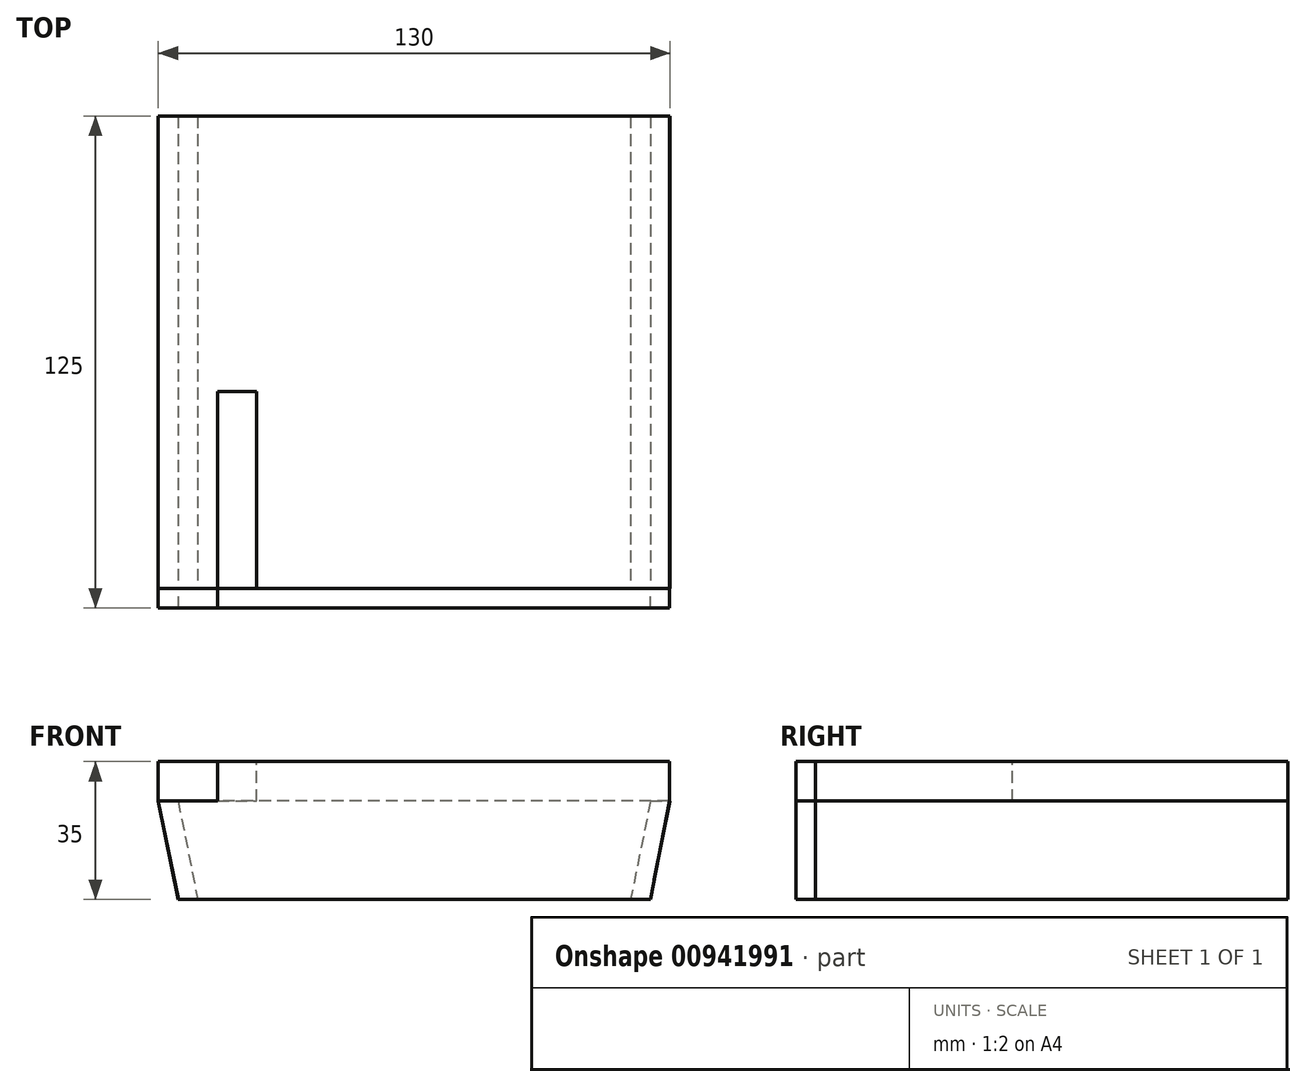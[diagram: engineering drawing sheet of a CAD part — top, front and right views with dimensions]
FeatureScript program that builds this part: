
annotation { "Feature Type Name" : "Feature", "Feature Type Description" : "" }
export const myFeature = defineFeature(function(context is Context, id is Id, definition is map)
    precondition{}
    {
        {
            var Q0;
            Q0=qCreatedBy(makeId("Top.planeOp"),FACE);
            var sketch = newSketch(context, id + "F0", { "sketchPlane" : qUnion([Q0])});
            skLineSegment(sketch, "E0", {"start": v(-47.45, 41.66) * mm, "end": v(62.55, 41.66) * mm});
            skLineSegment(sketch, "E1", {"start": v(62.55, 41.66) * mm, "end": v(62.55, -78.34) * mm});
            skLineSegment(sketch, "E2", {"start": v(62.55, -78.34) * mm, "end": v(-47.45, -78.34) * mm});
            skLineSegment(sketch, "E3", {"start": v(-47.45, -78.34) * mm, "end": v(-47.45, 41.66) * mm});
            skSolve(sketch);
        }
        {
            var Q0;
            Q0 = qSketchRegion(id + "F0", true);
            extrude(context, id + "F1", {"entities" : qUnion([Q0]), "depth" : 25 * mm, "offsetDistance" : 25 * mm});
        }
        {
            var Q0;
            Q0=makeQuery(id+"F1.opExtrude","SWEPT_FACE",FACE,{"disambiguationData":[OSD([sQuery(id+"F0.wireOp",EDGE,"E2")])]});
            var sketch = newSketch(context, id + "F2", { "sketchPlane" : qUnion([Q0])});
            skLineSegment(sketch, "E4", {"start": v(62.55, 25) * mm, "end": v(67.55, 25) * mm});
            skLineSegment(sketch, "E5", {"start": v(67.55, 25) * mm, "end": v(62.55, 0) * mm});
            skLineSegment(sketch, "E6", {"start": v(62.55, 0) * mm, "end": v(-47.45, 0) * mm});
            skLineSegment(sketch, "E7", {"start": v(62.55, 25) * mm, "end": v(-47.45, 25) * mm});
            skLineSegment(sketch, "E8", {"start": v(-47.45, 25) * mm, "end": v(-52.45, 25) * mm});
            skLineSegment(sketch, "E9", {"start": v(-52.45, 25) * mm, "end": v(-47.45, 0) * mm});
            skSolve(sketch);
        }
        {
            var Q0;
            Q0=makeQuery(id+"F2.imprint","IMPRINT",FACE,{"disambiguationData":[TD([[makeQuery(id+"F2.imprint","IMPRINT",EDGE,{"derivedFrom":sQuery(id+"F2.wireOp",EDGE,"E8")}),1.0]])]});
            var Q1;
            Q1=makeQuery(id+"F2.imprint","IMPRINT",FACE,{"disambiguationData":[TD([[makeQuery(id+"F2.imprint","IMPRINT",EDGE,{"derivedFrom":sQuery(id+"F2.wireOp",EDGE,"E6")}),-1.0]])]});
            var Q2;
            Q2=makeQuery(id+"F2.imprint","IMPRINT",FACE,{"disambiguationData":[TD([[makeQuery(id+"F2.imprint","IMPRINT",EDGE,{"derivedFrom":sQuery(id+"F2.wireOp",EDGE,"E4")}),-1.0]])]});
            extrude(context, id + "F3", {"entities" : qUnion([Q0, Q1, Q2]), "operationType" : NewBodyOperationType.ADD, "depth" : -120 * mm, "offsetDistance" : 25 * mm});
        }
        {
            var Q0;
            Q0=makeQuery(id+"F3.boolean.opBoolean","MERGE",FACE,{"derivedFrom":[makeQuery(id+"F1.opExtrude","SWEPT_FACE",FACE,{"disambiguationData":[OSD([sQuery(id+"F0.wireOp",EDGE,"E2")])]}),makeQuery(id+"F3.opExtrude","CAP_FACE",FACE,{"disambiguationData":[OSD([sQuery(id+"F2.wireOp",EDGE,"E4"),sQuery(id+"F2.wireOp",EDGE,"E5"),sQuery(id+"F2.wireOp",EDGE,"E6"),sQuery(id+"F2.wireOp",EDGE,"E7"),sQuery(id+"F2.wireOp",EDGE,"E8"),sQuery(id+"F2.wireOp",EDGE,"E9")])],"isStart":true})]});
            var sketch = newSketch(context, id + "F4", { "sketchPlane" : qUnion([Q0])});
            skLineSegment(sketch, "E10", {"start": v(62.55, 0) * mm, "end": v(67.55, 0) * mm});
            skLineSegment(sketch, "E11", {"start": v(67.55, 25) * mm, "end": v(72.55, 25) * mm});
            skLineSegment(sketch, "E12", {"start": v(72.55, 25) * mm, "end": v(67.55, 0) * mm});
            skLineSegment(sketch, "E13", {"start": v(67.55, 25) * mm, "end": v(62.55, 0) * mm});
            skLineSegment(sketch, "E14", {"start": v(-52.45, 25) * mm, "end": v(-57.45, 25) * mm});
            skLineSegment(sketch, "E15", {"start": v(-47.45, 0) * mm, "end": v(-52.45, 0) * mm});
            skLineSegment(sketch, "E16", {"start": v(-57.45, 25) * mm, "end": v(-52.45, 0) * mm});
            skSolve(sketch);
        }
        {
            var Q0;
            Q0=makeQuery(id+"F4.imprint","IMPRINT",FACE,{"disambiguationData":[TD([[makeQuery(id+"F4.imprint","IMPRINT",EDGE,{"derivedFrom":sQuery(id+"F4.wireOp",EDGE,"E10")}),1.0]])]});
            var Q1;
            Q1=makeQuery(id+"F4.imprint","IMPRINT",FACE,{"disambiguationData":[TD([[makeQuery(id+"F4.imprint","IMPRINT",EDGE,{"derivedFrom":sQuery(id+"F4.wireOp",EDGE,"E14")}),1.0]])]});
            extrude(context, id + "F5", {"entities" : qUnion([Q0, Q1]), "depth" : -120 * mm, "offsetDistance" : 25 * mm});
        }
        {
            var Q0;
            Q0=makeQuery(id+"F3.boolean.opBoolean","MERGE",FACE,{"derivedFrom":[makeQuery(id+"F1.opExtrude","SWEPT_FACE",FACE,{"disambiguationData":[OSD([sQuery(id+"F0.wireOp",EDGE,"E2")])]}),makeQuery(id+"F3.opExtrude","CAP_FACE",FACE,{"disambiguationData":[OSD([sQuery(id+"F2.wireOp",EDGE,"E4"),sQuery(id+"F2.wireOp",EDGE,"E5"),sQuery(id+"F2.wireOp",EDGE,"E6"),sQuery(id+"F2.wireOp",EDGE,"E7"),sQuery(id+"F2.wireOp",EDGE,"E8"),sQuery(id+"F2.wireOp",EDGE,"E9")])],"isStart":true})]});
            extrude(context, id + "F6", {"entities" : qUnion([Q0]), "operationType" : NewBodyOperationType.REMOVE, "oppositeDirection" : true, "depth" : 120 * mm, "offsetDistance" : 25 * mm});
        }
        {
            var Q0;
            Q0=makeQuery(id+"F5.opExtrude","SWEPT_FACE",FACE,{"disambiguationData":[OSD([sQuery(id+"F4.wireOp",EDGE,"E14")])]});
            var sketch = newSketch(context, id + "F7", { "sketchPlane" : qUnion([Q0])});
            skLineSegment(sketch, "E17", {"start": v(-57.45, -78.34) * mm, "end": v(72.37, -78.34) * mm});
            skLineSegment(sketch, "E18", {"start": v(72.37, -78.34) * mm, "end": v(72.37, 41.66) * mm});
            skLineSegment(sketch, "E19", {"start": v(72.37, 41.66) * mm, "end": v(-52.45, 41.66) * mm});
            skLineSegment(sketch, "E20", {"start": v(-52.45, 41.66) * mm, "end": v(-57.45, 41.66) * mm});
            skLineSegment(sketch, "E21", {"start": v(-57.45, 41.66) * mm, "end": v(-57.45, -78.34) * mm});
            skSolve(sketch);
        }
        {
            var Q0;
            Q0=makeQuery(id+"F7.imprint","IMPRINT",FACE,{"disambiguationData":[TD([[makeQuery(id+"F7.imprint","IMPRINT",EDGE,{"derivedFrom":sQuery(id+"F7.wireOp",EDGE,"E20")}),1.0]])]});
            var Q1;
            {var subQ2=sQuery(id+"F7.wireOp",EDGE,"E18");Q1=makeQuery(id+"F7.imprint","IMPRINT",FACE,{"disambiguationData":[TD([[makeQuery(id+"F7.imprint","IMPRINT",EDGE,{"derivedFrom":subQ2}),1.0]])]});}
            extrude(context, id + "F8", {"entities" : qUnion([Q0, Q1]), "depth" : 5 * mm, "offsetDistance" : 25 * mm});
        }
        {
            var Q0;
            Q0=makeQuery(id+"F8.opExtrude","CAP_FACE",FACE,{"disambiguationData":[OSD([sQuery(id+"F7.wireOp",EDGE,"E17"),sQuery(id+"F7.wireOp",EDGE,"E18"),sQuery(id+"F7.wireOp",EDGE,"E19"),sQuery(id+"F7.wireOp",EDGE,"E20"),sQuery(id+"F7.wireOp",EDGE,"E21")])],"isStart":false});
            var sketch = newSketch(context, id + "F9", { "sketchPlane" : qUnion([Q0])});
            skLineSegment(sketch, "E22", {"start": v(-57.45, -78.34) * mm, "end": v(-42.45, -78.34) * mm});
            skLineSegment(sketch, "E23", {"start": v(-42.45, -78.34) * mm, "end": v(-42.45, -28.34) * mm});
            skLineSegment(sketch, "E24", {"start": v(-42.45, -28.34) * mm, "end": v(-32.45, -28.34) * mm});
            skLineSegment(sketch, "E25", {"start": v(-32.45, -28.34) * mm, "end": v(-32.45, -78.34) * mm});
            skLineSegment(sketch, "E26", {"start": v(-32.45, -78.34) * mm, "end": v(-42.45, -78.34) * mm});
            skSolve(sketch);
        }
        {
            var Q0;
            Q0 = qSketchRegion(id + "F9", true);
            extrude(context, id + "F10", {"entities" : qUnion([Q0]), "operationType" : NewBodyOperationType.REMOVE, "oppositeDirection" : true, "depth" : 25 * mm, "offsetDistance" : 25 * mm});
        }
        {
            var Q0;
            Q0=makeQuery(id+"F8.opExtrude","CAP_FACE",FACE,{"disambiguationData":[OSD([sQuery(id+"F7.wireOp",EDGE,"E17"),sQuery(id+"F7.wireOp",EDGE,"E18"),sQuery(id+"F7.wireOp",EDGE,"E19"),sQuery(id+"F7.wireOp",EDGE,"E20"),sQuery(id+"F7.wireOp",EDGE,"E21")])],"isStart":false});
            var sketch = newSketch(context, id + "F11", { "sketchPlane" : qUnion([Q0])});
            skLineSegment(sketch, "E27", {"start": v(-57.45, -78.34) * mm, "end": v(72.37, -78.34) * mm});
            skLineSegment(sketch, "E28", {"start": v(72.37, -78.34) * mm, "end": v(72.37, 41.66) * mm});
            skLineSegment(sketch, "E29", {"start": v(72.37, 41.66) * mm, "end": v(-57.45, 41.66) * mm});
            skLineSegment(sketch, "E30", {"start": v(-57.45, 41.66) * mm, "end": v(-57.45, -78.34) * mm});
            skSolve(sketch);
        }
        {
            var Q0;
            {var subQ1=makeQuery(id+"F10.boolean.opBoolean","COPY",EDGE,{"derivedFrom":makeQuery(id+"F10.opExtrude","CAP_EDGE",EDGE,{"disambiguationData":[OSD([sQuery(id+"F9.wireOp",EDGE,"E23")])],"isStart":true})});Q0=makeQuery(id+"F11.imprint","IMPRINT",FACE,{"disambiguationData":[TD([[makeQuery(id+"F11.imprint","IMPRINT",EDGE,{"derivedFrom":subQ1}),-1.0]])]});}
            var Q1;
            {var subQ0=sQuery(id+"F11.wireOp",EDGE,"E28");Q1=makeQuery(id+"F11.imprint","IMPRINT",FACE,{"disambiguationData":[TD([[makeQuery(id+"F11.imprint","IMPRINT",EDGE,{"derivedFrom":subQ0}),1.0]])]});}
            extrude(context, id + "F12", {"entities" : qUnion([Q0, Q1]), "operationType" : NewBodyOperationType.ADD, "depth" : 5 * mm, "offsetDistance" : 25 * mm});
        }
        {
            var Q0;
            {var subQ0=sQuery(id+"F7.wireOp",EDGE,"E21");var subQ3=sQuery(id+"F7.wireOp",EDGE,"E18");var subQ4=sQuery(id+"F7.wireOp",EDGE,"E17");var subQ7=makeQuery(id+"F8.opExtrude","SWEPT_FACE",FACE,{"disambiguationData":[OSD([subQ4])]});Q0=makeQuery(id+"F12.boolean.opBoolean","MERGE",FACE,{"derivedFrom":[makeQuery(id+"F10.boolean.opBoolean","SPLIT",FACE,{"disambiguationData":[TD([makeQuery(id+"F8.opExtrude","SWEPT_FACE",FACE,{"disambiguationData":[OSD([subQ0])]})])],"derivedFrom":subQ7}),makeQuery(id+"F10.boolean.opBoolean","SPLIT",FACE,{"disambiguationData":[TD([makeQuery(id+"F8.opExtrude","SWEPT_FACE",FACE,{"disambiguationData":[OSD([subQ3])]})])],"derivedFrom":subQ7}),makeQuery(id+"F12.opExtrude","SWEPT_FACE",FACE,{"disambiguationData":[OSD([sQuery(id+"F11.wireOp",EDGE,"E27")])]})]});}
            var sketch = newSketch(context, id + "F13", { "sketchPlane" : qUnion([Q0])});
            skLineSegment(sketch, "E31", {"start": v(-57.45, 35) * mm, "end": v(72.37, 35) * mm});
            skLineSegment(sketch, "E32", {"start": v(72.37, 35) * mm, "end": v(72.37, 25) * mm});
            skLineSegment(sketch, "E33", {"start": v(72.37, 25) * mm, "end": v(67.6, 0) * mm});
            skLineSegment(sketch, "E34", {"start": v(67.6, 0) * mm, "end": v(-52.36, 0) * mm});
            skLineSegment(sketch, "E35", {"start": v(-52.36, 0) * mm, "end": v(-57.45, 25) * mm});
            skLineSegment(sketch, "E36", {"start": v(-57.45, 25) * mm, "end": v(-57.45, 35) * mm});
            skSolve(sketch);
        }
        {
            var Q0;
            Q0=makeQuery(id+"F13.imprint","IMPRINT",FACE,{"disambiguationData":[TD([[makeQuery(id+"F13.imprint","IMPRINT",EDGE,{"derivedFrom":sQuery(id+"F13.wireOp",EDGE,"E31")}),-1.0]])]});
            var Q1;
            Q1=makeQuery(id+"F13.imprint","IMPRINT",FACE,{"disambiguationData":[TD([[makeQuery(id+"F13.imprint","IMPRINT",EDGE,{"derivedFrom":sQuery(id+"F13.wireOp",EDGE,"E33")}),-1.0]])]});
            extrude(context, id + "F14", {"entities" : qUnion([Q0, Q1]), "depth" : 5 * mm, "offsetDistance" : 25 * mm});
        }
    });
